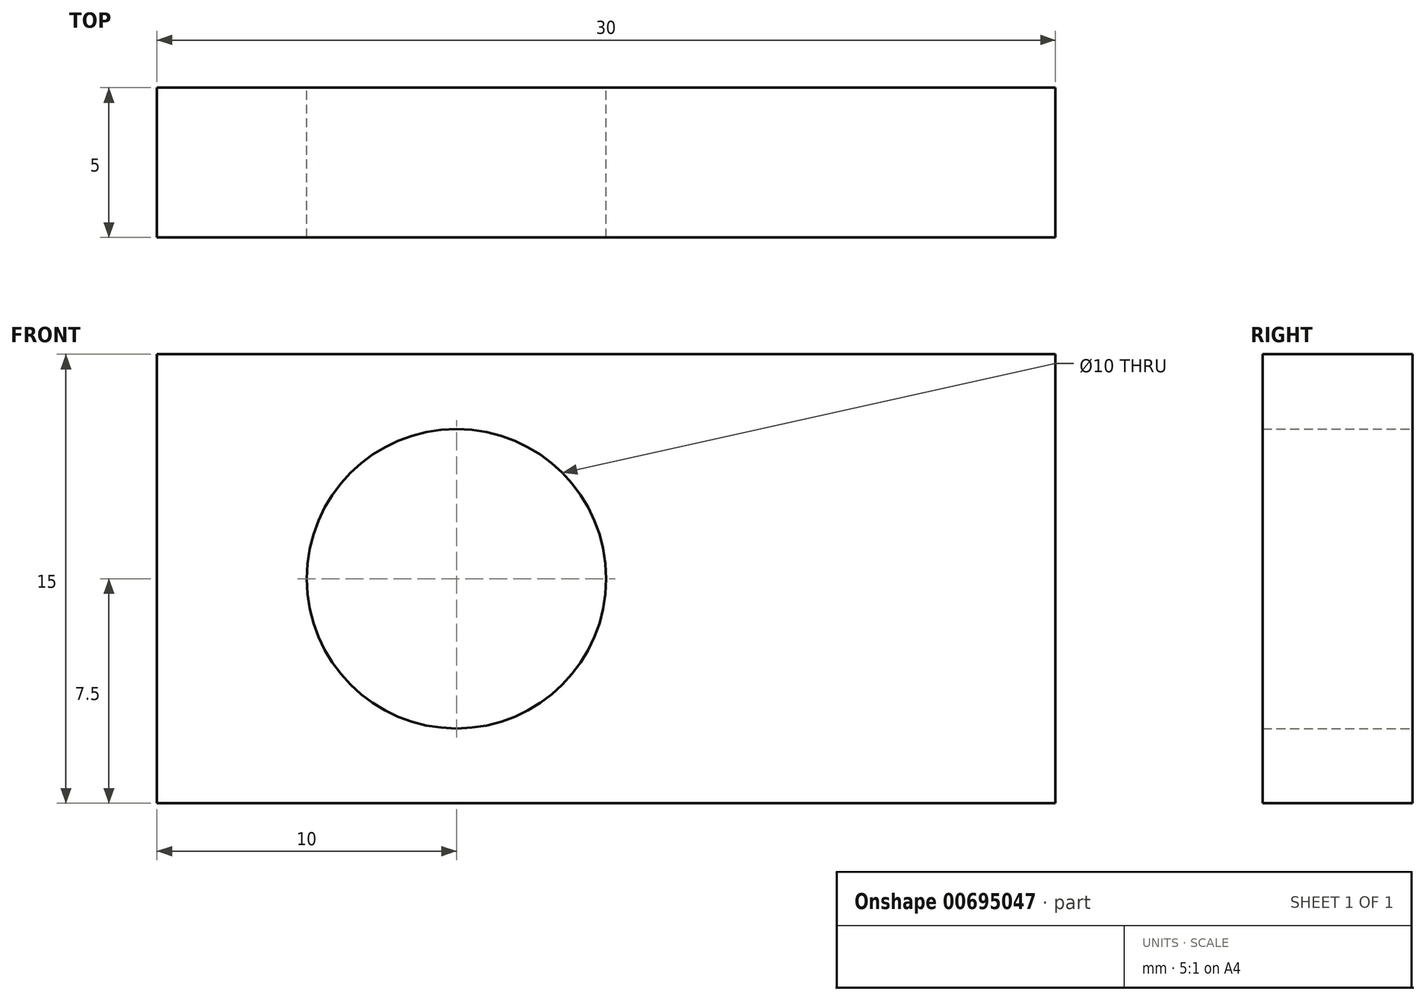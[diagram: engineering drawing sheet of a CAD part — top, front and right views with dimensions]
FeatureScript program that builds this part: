
annotation { "Feature Type Name" : "Feature", "Feature Type Description" : "" }
export const myFeature = defineFeature(function(context is Context, id is Id, definition is map)
    precondition{}
    {
        {
            var Q0;
            Q0=qCreatedBy(makeId("Front.planeOp"),FACE);
            var sketch = newSketch(context, id + "F0", { "sketchPlane" : qUnion([Q0])});
            skLineSegment(sketch, "E0.bottom", {"start": v(0, 0) * mm, "end": v(30, 0) * mm});
            skLineSegment(sketch, "E0.top", {"start": v(0, 15) * mm, "end": v(30, 15) * mm});
            skLineSegment(sketch, "E0.left", {"start": v(0, 0) * mm, "end": v(0, 15) * mm});
            skLineSegment(sketch, "E0.right", {"start": v(30, 0) * mm, "end": v(30, 15) * mm});
            skLineSegment(sketch, "E1", {"start": v(-13.1, 7.5) * mm, "end": v(75.63, 7.5) * mm, "construction": true});
            skPoint(sketch, "E1.startSnap0", {"position": v(0, 7.5) * mm});
            skCircle(sketch, "E2", {"center": v(10, 7.5) * mm, "radius": 5 * mm});
            skSolve(sketch);
        }
        {
            var Q0;
            Q0 = qSketchRegion(id + "F0", true);
            extrude(context, id + "F1", {"entities" : qUnion([Q0]), "depth" : 5 * mm, "offsetDistance" : 25 * mm});
        }
    });
